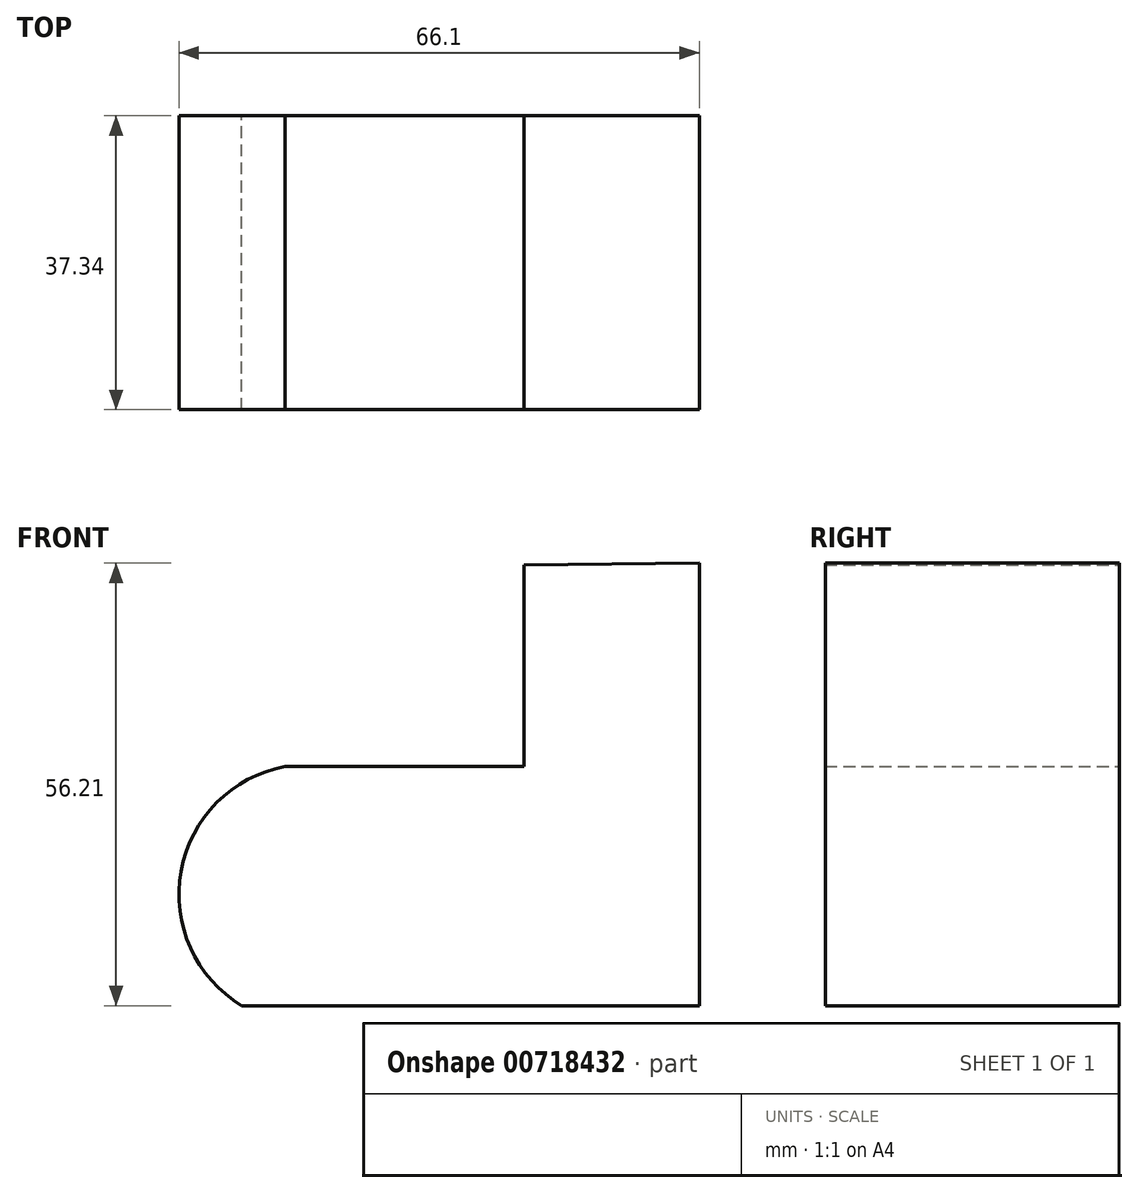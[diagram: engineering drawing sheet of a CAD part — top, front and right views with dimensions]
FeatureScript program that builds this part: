
annotation { "Feature Type Name" : "Feature", "Feature Type Description" : "" }
export const myFeature = defineFeature(function(context is Context, id is Id, definition is map)
    precondition{}
    {
        {
            var Q0;
            Q0=qCreatedBy(makeId("Front.planeOp"),FACE);
            var sketch = newSketch(context, id + "F0", { "sketchPlane" : qUnion([Q0])});
            skLineSegment(sketch, "E0", {"start": v(40.3, 56.21) * mm, "end": v(40.3, 0) * mm});
            skLineSegment(sketch, "E1", {"start": v(40.3, 0) * mm, "end": v(-22.84, 0) * mm});
            skArc(sketch, "E2", {"start": v(-12.32, 30.38) * mm, "mid": v(-25.54, 17.08) * mm, "end": v(-17.82, 0) * mm});
            skLineSegment(sketch, "E3", {"start": v(-12.32, 30.38) * mm, "end": v(18.06, 30.38) * mm});
            skLineSegment(sketch, "E4", {"start": v(18.06, 30.38) * mm, "end": v(18.06, 55.97) * mm});
            skLineSegment(sketch, "E5", {"start": v(18.06, 55.97) * mm, "end": v(40.3, 56.21) * mm});
            skSolve(sketch);
        }
        {
            var Q0;
            Q0 = qSketchRegion(id + "F0", true);
            extrude(context, id + "F1", {"entities" : qUnion([Q0]), "depth" : 37.34 * mm, "offsetDistance" : 25.4 * mm});
        }
    });
